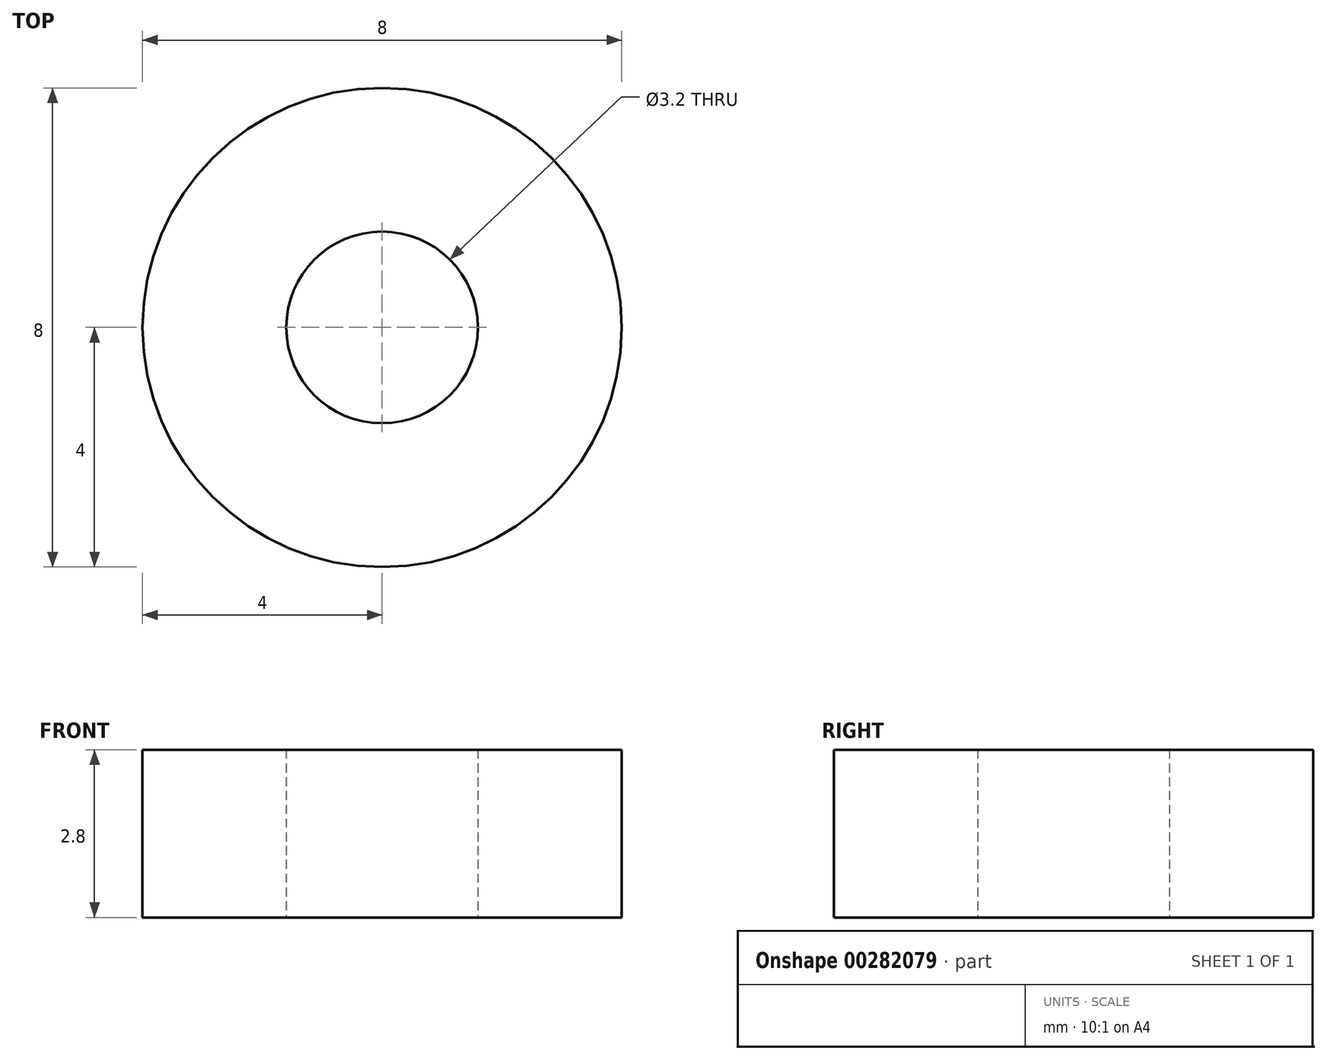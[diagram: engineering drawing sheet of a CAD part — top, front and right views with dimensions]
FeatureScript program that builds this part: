
annotation { "Feature Type Name" : "Feature", "Feature Type Description" : "" }
export const myFeature = defineFeature(function(context is Context, id is Id, definition is map)
    precondition{}
    {
        {
            var Q0;
            Q0=qCreatedBy(makeId("Top.planeOp"),FACE);
            var sketch = newSketch(context, id + "F0", { "sketchPlane" : qUnion([Q0])});
            skCircle(sketch, "E0", {"center": v(0, 0) * mm, "radius": 4 * mm});
            skCircle(sketch, "E1", {"center": v(0, 0) * mm, "radius": 1.6 * mm});
            skSolve(sketch);
        }
        {
            var Q0;
            Q0=makeQuery(id+"F0.imprint","IMPRINT",FACE,{"disambiguationData":[TD([[makeQuery(id+"F0.imprint","IMPRINT",EDGE,{"derivedFrom":sQuery(id+"F0.wireOp",EDGE,"E0")}),1.0]])]});
            extrude(context, id + "F1", {"entities" : qUnion([Q0]), "depth" : 2.8 * mm});
        }
    });
